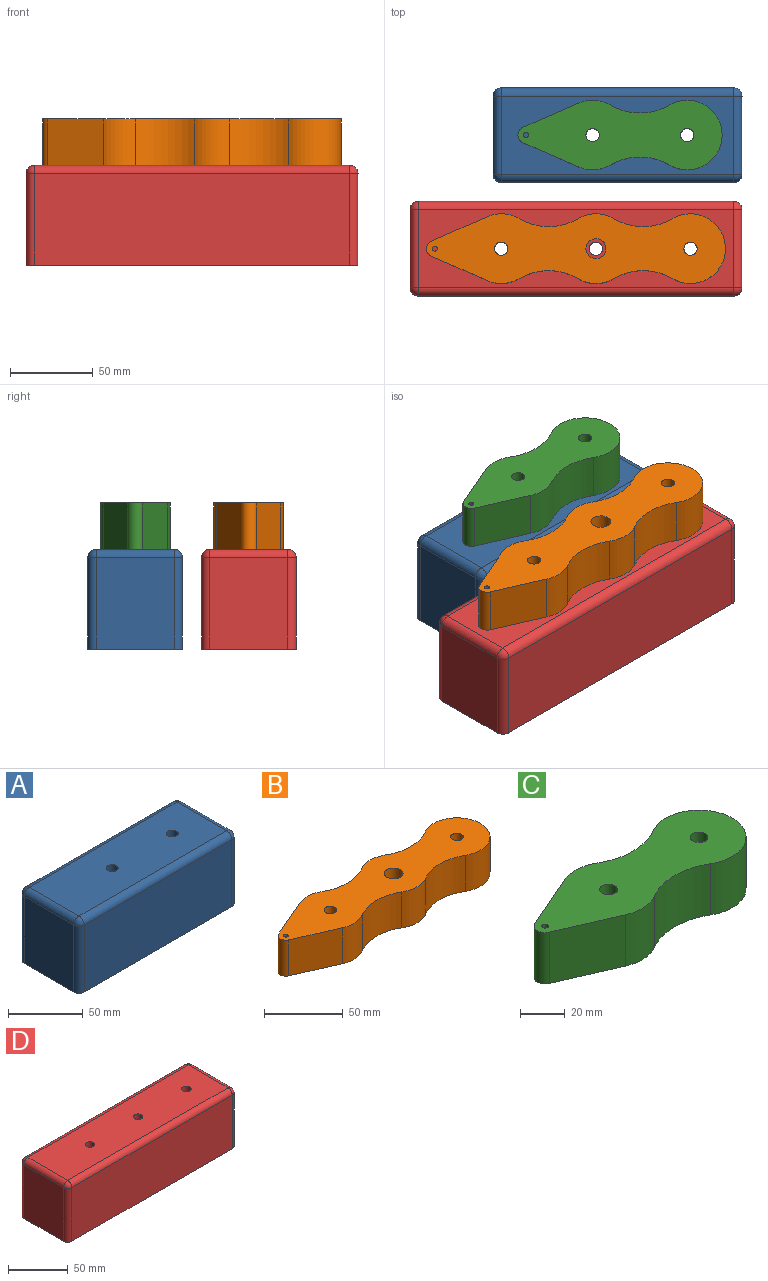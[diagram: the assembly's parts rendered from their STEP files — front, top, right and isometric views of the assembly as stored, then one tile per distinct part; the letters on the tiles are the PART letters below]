
ASSEMBLY  parts=4 mates=5
PART A: 20 faces, bbox 150x57x60 mm
  f0: plane 55x47mm, normal (-1,0,0), area 2585mm2, adj f7,f10,f16,f19
  f1: plane 140x55mm, normal (0,-1,0), area 7700mm2, adj f7,f13,f17,f19
  f2: plane 55x47mm, normal (1,0,0), area 2585mm2, adj f7,f8,f12,f13
  f3: cylinder r=4mm len=60mm, axis (0,0,-1), area 1508mm2, adj f6,f7
  f4: plane 140x55mm, normal (0,1,0), area 7700mm2, adj f7,f8,f10,f11
  f5: cylinder r=4mm len=60mm, axis (0,0,-1), area 1508mm2, adj f6,f7
  f6: plane 140x47mm, normal (0,0,1), area 6479.5mm2, adj f3,f5,f11,f12,f16,f17
  f7: plane 150x57mm, normal (0,0,-1), area 8428mm2, adj f0,f1,f2,f3,f4,f5,f8,f10
  f8: cylinder r=5mm len=55mm, axis (0,0,1), area 432mm2, adj f2,f4,f7,f9
  f9: sphere r=5mm, area 39.3mm2, adj f8,f11,f12
  f10: cylinder r=5mm len=55mm, axis (0,0,-1), area 432mm2, adj f0,f4,f7,f14
  f11: cylinder r=5mm len=140mm, axis (1,0,0), area 1099.6mm2, adj f4,f6,f9,f14
  f12: cylinder r=5mm len=47mm, axis (0,-1,0), area 369.1mm2, adj f2,f6,f9,f15
  f13: cylinder r=5mm len=55mm, axis (0,0,-1), area 432mm2, adj f1,f2,f7,f15
  f14: sphere r=5mm, area 39.3mm2, adj f10,f11,f16
  f15: sphere r=5mm, area 39.3mm2, adj f12,f13,f17
  f16: cylinder r=5mm len=47mm, axis (0,1,0), area 369.1mm2, adj f0,f6,f14,f18
  f17: cylinder r=5mm len=140mm, axis (-1,0,0), area 1099.6mm2, adj f1,f6,f15,f18
  f18: sphere r=5mm, area 39.3mm2, adj f16,f17,f19
  f19: cylinder r=5mm len=55mm, axis (0,0,1), area 432mm2, adj f0,f1,f7,f18
PART B: 18 faces, bbox 180x42x28 mm
  f0: cylinder r=21mm len=28mm, axis (0,0,-1), area 555.2mm2, adj f1,f15,f16,f17
  f1: cylinder r=35.12mm len=35.67mm, axis (0,0,-1), area 1047.6mm2, adj f0,f2,f16,f17
  f2: cylinder r=21mm len=28mm, axis (0,0,-1), area 626.4mm2, adj f1,f3,f16,f17
  f3: cylinder r=35.12mm len=35.67mm, axis (0,0,-1), area 1047.6mm2, adj f2,f4,f16,f17
  f4: cylinder r=21mm len=42mm, axis (0,0,-1), area 2473.7mm2, adj f3,f5,f16,f17
  f5: cylinder r=35.12mm len=35.67mm, axis (0,0,-1), area 1047.6mm2, adj f4,f6,f16,f17
  f6: cylinder r=21mm len=28mm, axis (0,0,-1), area 626.4mm2, adj f5,f7,f16,f17
  f7: cylinder r=35.12mm len=35.67mm, axis (0,0,-1), area 1047.6mm2, adj f6,f8,f16,f17
  f8: cylinder r=21mm len=28mm, axis (0,0,-1), area 555.2mm2, adj f7,f9,f16,f17
  f9: plane 33.6x28mm, normal (-0.4,0.92,0), area 1026.5mm2, adj f8,f10,f16,f17
  f10: cylinder r=5mm len=28mm, axis (0,0,-1), area 324.6mm2, adj f9,f15,f16,f17
  f11: cylinder r=4mm len=28mm, axis (0,0,-1), area 703.7mm2, adj f16,f17
  f12: cylinder r=6mm len=28mm, axis (0,0,-1), area 1055.6mm2, adj f16,f17
  f13: cylinder r=4mm len=28mm, axis (0,0,-1), area 703.7mm2, adj f16,f17
  f14: cylinder r=1.5mm len=28mm, axis (0,0,-1), area 263.9mm2, adj f16,f17
  f15: plane 33.6x28mm, normal (-0.4,-0.92,0), area 1026.5mm2, adj f0,f10,f16,f17
  f16: plane 180x42mm, normal (0,0,1), area 5458.5mm2, adj f0,f1,f2,f3,f4,f5,f6,f7
  f17: plane 180x42mm, normal (0,0,-1), area 5458.5mm2, adj f0,f1,f2,f3,f4,f5,f6,f7
PART C: 13 faces, bbox 123x42x28 mm
  f0: cylinder r=5mm len=28mm, axis (0,0,-1), area 324.6mm2, adj f1,f10,f11,f12
  f1: plane 33.6x28mm, normal (-0.4,-0.92,0), area 1026.5mm2, adj f0,f2,f11,f12
  f2: cylinder r=21mm len=28mm, axis (0,0,-1), area 555.2mm2, adj f1,f3,f11,f12
  f3: cylinder r=35.12mm len=35.67mm, axis (0,0,-1), area 1047.6mm2, adj f2,f4,f11,f12
  f4: cylinder r=21mm len=42mm, axis (0,0,-1), area 2473.7mm2, adj f3,f5,f11,f12
  f5: cylinder r=35.12mm len=35.67mm, axis (0,0,-1), area 1047.6mm2, adj f4,f6,f11,f12
  f6: cylinder r=21mm len=28mm, axis (0,0,-1), area 555.2mm2, adj f5,f10,f11,f12
  f7: cylinder r=4mm len=28mm, axis (0,0,-1), area 703.7mm2, adj f11,f12
  f8: cylinder r=4mm len=28mm, axis (0,0,-1), area 703.7mm2, adj f11,f12
  f9: cylinder r=1.5mm len=28mm, axis (0,0,-1), area 263.9mm2, adj f11,f12
  f10: plane 33.6x28mm, normal (-0.4,0.92,0), area 1026.5mm2, adj f0,f6,f11,f12
  f11: plane 123x42mm, normal (0,0,1), area 3660.2mm2, adj f0,f1,f2,f3,f4,f5,f6,f7
  f12: plane 123x42mm, normal (0,0,-1), area 3660.2mm2, adj f0,f1,f2,f3,f4,f5,f6,f7
PART D: 21 faces, bbox 200x57x60 mm
  f0: plane 55x47mm, normal (-1,0,0), area 2585mm2, adj f8,f11,f17,f20
  f1: plane 190x55mm, normal (0,-1,0), area 10450mm2, adj f8,f14,f18,f20
  f2: plane 55x47mm, normal (1,0,0), area 2585mm2, adj f8,f9,f13,f14
  f3: cylinder r=4mm len=60mm, axis (0,0,-1), area 1508mm2, adj f7,f8
  f4: cylinder r=4mm len=60mm, axis (0,0,-1), area 1508mm2, adj f7,f8
  f5: plane 190x55mm, normal (0,1,0), area 10450mm2, adj f8,f9,f11,f12
  f6: cylinder r=4mm len=60mm, axis (0,0,-1), area 1508mm2, adj f7,f8
  f7: plane 190x47mm, normal (0,0,1), area 8779.2mm2, adj f3,f4,f6,f12,f13,f17,f18
  f8: plane 200x57mm, normal (0,0,-1), area 11227.7mm2, adj f0,f1,f2,f3,f4,f5,f6,f9
  f9: cylinder r=5mm len=55mm, axis (0,0,1), area 432mm2, adj f2,f5,f8,f10
  f10: sphere r=5mm, area 39.3mm2, adj f9,f12,f13
  f11: cylinder r=5mm len=55mm, axis (0,0,-1), area 432mm2, adj f0,f5,f8,f15
  f12: cylinder r=5mm len=190mm, axis (1,0,0), area 1492.3mm2, adj f5,f7,f10,f15
  f13: cylinder r=5mm len=47mm, axis (0,-1,0), area 369.1mm2, adj f2,f7,f10,f16
  f14: cylinder r=5mm len=55mm, axis (0,0,-1), area 432mm2, adj f1,f2,f8,f16
  f15: sphere r=5mm, area 39.3mm2, adj f11,f12,f17
  f16: sphere r=5mm, area 39.3mm2, adj f13,f14,f18
  f17: cylinder r=5mm len=47mm, axis (0,1,0), area 369.1mm2, adj f0,f7,f15,f19
  f18: cylinder r=5mm len=190mm, axis (-1,0,0), area 1492.3mm2, adj f1,f7,f16,f19
  f19: sphere r=5mm, area 39.3mm2, adj f17,f18,f20
  f20: cylinder r=5mm len=55mm, axis (0,0,1), area 432mm2, adj f0,f1,f8,f19
PLACE A t=(-12.98,-15.76,-43.06)mm
PLACE B t=(106.02,-55.71,16.94)mm
PLACE C t=(161.02,12.74,16.94)mm
PLACE D t=(-62.98,-84.21,-43.06)mm
MATE planar C.f4 <-> A.f6  axis (0,0,-1) through (104.02,12.74,16.94)mm
MATE cylindrical C.f4 <-> A.f5  axis (0,0,-1) through (104.02,12.74,16.94)mm
MATE planar B.f17 <-> D.f7  axis (0,0,-1) through (41.75,-55.71,16.94)mm
MATE planar A.f2 <-> D.f2  axis (1,0,0) through (137.02,12.74,-15.56)mm
MATE cylindrical B.f4 <-> D.f6  axis (0,0,-1) through (106.02,-55.71,16.94)mm
